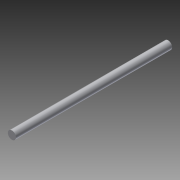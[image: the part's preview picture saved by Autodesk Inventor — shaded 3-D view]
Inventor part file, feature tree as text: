
AUTODESK INVENTOR PART (.ipt)
format: ipt  version: 2016 SP1 (Build 200210100, 210)  size: 79,872 bytes
history: native  units: in
note: dims shown in document units (in); Inventor stores cm internally (conversion verified against a paired STEP export)
features: extrude x1, sketch x1
ambient origin geometry x8: Origin, YZ Plane, XZ Plane, XY Plane, X Axis, Y Axis, Z Axis, Center Point
bodies: Solid1 (feature_tree)
feature tree (2):
  extrude  "Extrusion1"  Depth=12.0in TaperAngle=0.0deg
  sketch  "Sketch1"  dims[d0=0.625in d1=12.0in d2=0.0in]
